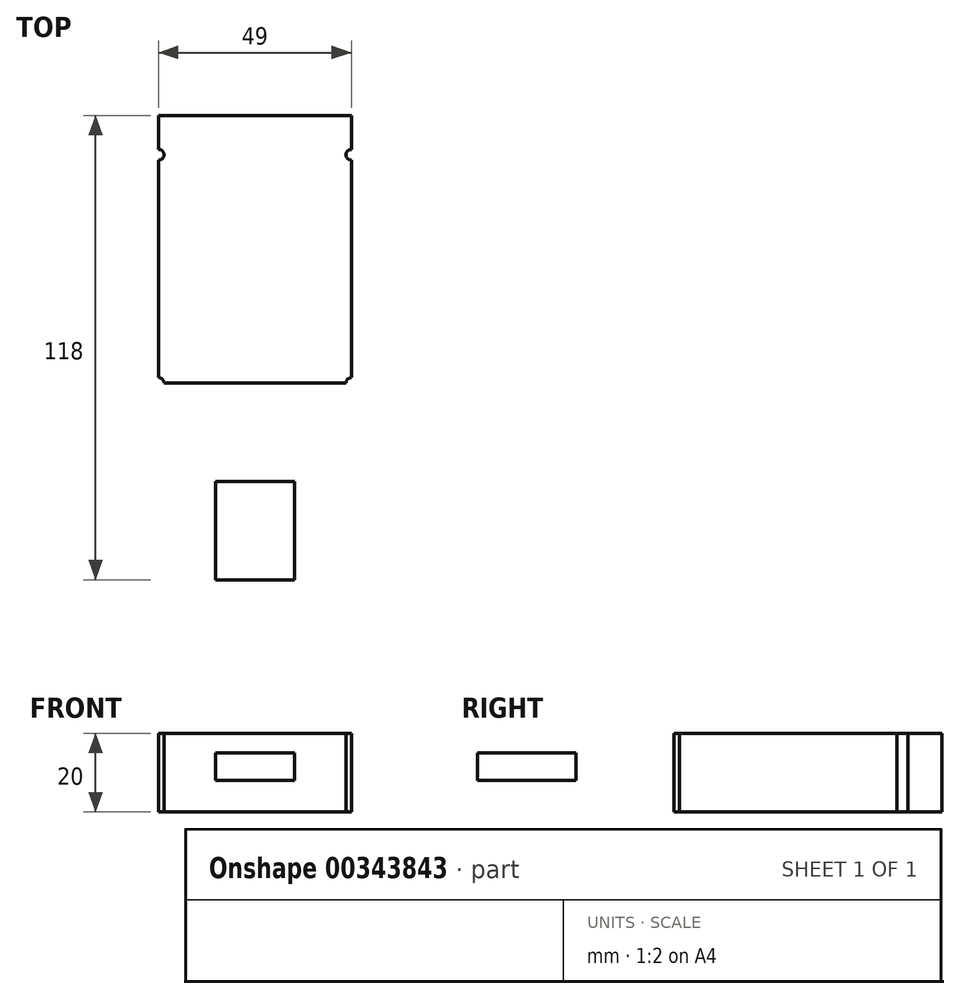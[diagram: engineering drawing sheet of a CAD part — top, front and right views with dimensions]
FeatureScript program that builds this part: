
annotation { "Feature Type Name" : "Feature", "Feature Type Description" : "" }
export const myFeature = defineFeature(function(context is Context, id is Id, definition is map)
    precondition{}
    {
        {
            var Q0;
            Q0=qCreatedBy(makeId("Top.planeOp"),FACE);
            var sketch = newSketch(context, id + "F0", { "sketchPlane" : qUnion([Q0])});
            skCircle(sketch, "E0", {"center": v(-14.65, 9.6) * mm, "radius": 1.37 * mm});
            skCircle(sketch, "E1", {"center": v(-14.65, -48.4) * mm, "radius": 1.38 * mm});
            skCircle(sketch, "E2", {"center": v(-63.65, -48.4) * mm, "radius": 1.38 * mm});
            skCircle(sketch, "E3", {"center": v(-63.65, 9.6) * mm, "radius": 1.38 * mm});
            skLineSegment(sketch, "E4.bottom", {"start": v(-14.65, 9.6) * mm, "end": v(-63.65, 9.6) * mm});
            skLineSegment(sketch, "E4.top", {"start": v(-14.65, -48.4) * mm, "end": v(-63.65, -48.4) * mm});
            skLineSegment(sketch, "E4.left", {"start": v(-14.65, 9.6) * mm, "end": v(-14.65, -48.4) * mm});
            skLineSegment(sketch, "E4.right", {"start": v(-63.65, 9.6) * mm, "end": v(-63.65, -48.4) * mm});
            skLineSegment(sketch, "E5.top", {"start": v(-14.65, -73.4) * mm, "end": v(-63.65, -73.4) * mm});
            skLineSegment(sketch, "E5.left", {"start": v(-14.65, -48.4) * mm, "end": v(-14.65, -73.4) * mm});
            skLineSegment(sketch, "E5.right", {"start": v(-63.65, -48.4) * mm, "end": v(-63.65, -73.4) * mm});
            skLineSegment(sketch, "E6.bottom", {"start": v(-63.65, 9.6) * mm, "end": v(-14.65, 9.6) * mm});
            skLineSegment(sketch, "E6.top", {"start": v(-63.65, 19.6) * mm, "end": v(-14.65, 19.6) * mm});
            skLineSegment(sketch, "E6.left", {"start": v(-63.65, 9.6) * mm, "end": v(-63.65, 19.6) * mm});
            skLineSegment(sketch, "E6.right", {"start": v(-14.65, 9.6) * mm, "end": v(-14.65, 19.6) * mm});
            skLineSegment(sketch, "E7.bottom", {"start": v(-49.15, -98.4) * mm, "end": v(-29.15, -98.4) * mm});
            skLineSegment(sketch, "E7.left", {"start": v(-49.15, -98.4) * mm, "end": v(-49.15, -73.4) * mm});
            skLineSegment(sketch, "E7.right", {"start": v(-29.15, -98.4) * mm, "end": v(-29.15, -73.4) * mm});
            skPoint(sketch, "E7.middle", {"position": v(-39.15, -73.4) * mm});
            skPoint(sketch, "E8", {"position": v(-49.15, -73.4) * mm});
            skPoint(sketch, "E9", {"position": v(-29.15, -73.4) * mm});
            skLineSegment(sketch, "E10", {"start": v(-49.15, -73.4) * mm, "end": v(-29.15, -73.4) * mm});
            skSolve(sketch);
        }
        {
            var Q0;
            {var subQ0=sQuery(id+"F0.wireOp",EDGE,"E4.left");var subQ13=sQuery(id+"F0.wireOp",EDGE,"E0");var subQ15=makeQuery(id+"F0.imprint","INTERSECT",VERTEX,{"derivedFrom":[subQ13,subQ0]});Q0=makeQuery(id+"F0.imprint","IMPRINT",FACE,{"disambiguationData":[TD([[makeQuery(id+"F0.imprint","IMPRINT",EDGE,{"disambiguationData":[TD([[subQ15,1.0]])],"derivedFrom":subQ13}),-1.0]])]});}
            var Q1;
            {var subQ7=sQuery(id+"F0.wireOp",EDGE,"E6.top");Q1=makeQuery(id+"F0.imprint","IMPRINT",FACE,{"disambiguationData":[TD([[makeQuery(id+"F0.imprint","IMPRINT",EDGE,{"derivedFrom":subQ7}),-1.0]])]});}
            var Q2;
            {var subQ3=sQuery(id+"F0.wireOp",EDGE,"E10");Q2=makeQuery(id+"F0.imprint","IMPRINT",FACE,{"disambiguationData":[TD([[makeQuery(id+"F0.imprint","IMPRINT",EDGE,{"derivedFrom":subQ3}),1.0]])]});}
            extrude(context, id + "F1", {"entities" : qUnion([Q0, Q1, Q2]), "depth" : 20 * mm, "offsetDistance" : 25 * mm});
        }
        {
            var Q0;
            Q0=makeQuery(id+"F0.imprint","IMPRINT",FACE,{"disambiguationData":[TD([[makeQuery(id+"F0.imprint","IMPRINT",EDGE,{"derivedFrom":sQuery(id+"F0.wireOp",EDGE,"E7.bottom")}),1.0]])]});
            extrude(context, id + "F2", {"entities" : qUnion([Q0]), "operationType" : NewBodyOperationType.ADD, "depth" : 15 * mm, "offsetDistance" : 25 * mm});
        }
        {
            var Q0;
            Q0=makeQuery(id+"F0.imprint","IMPRINT",FACE,{"disambiguationData":[TD([[makeQuery(id+"F0.imprint","IMPRINT",EDGE,{"derivedFrom":sQuery(id+"F0.wireOp",EDGE,"E7.bottom")}),1.0]])]});
            extrude(context, id + "F3", {"entities" : qUnion([Q0]), "operationType" : NewBodyOperationType.REMOVE, "depth" : 8 * mm, "offsetDistance" : 25 * mm});
        }
    });
